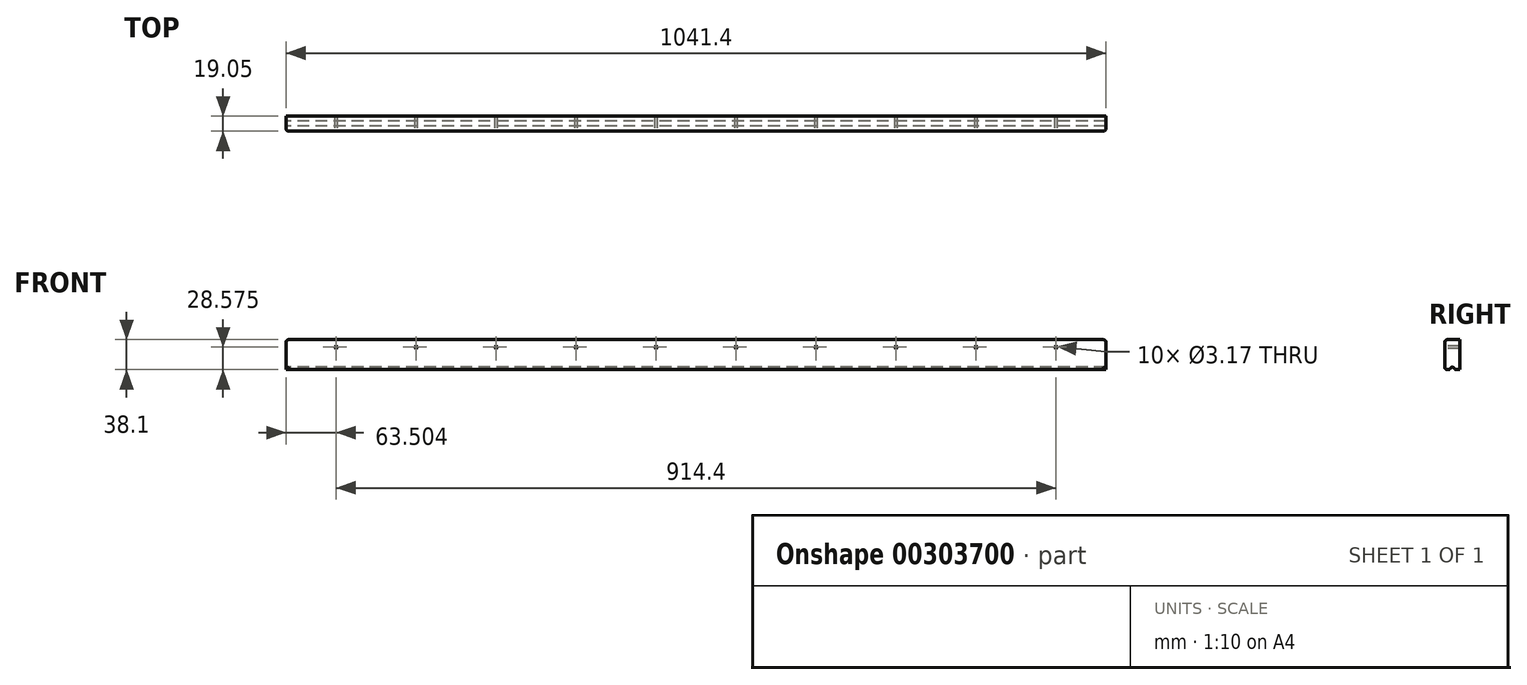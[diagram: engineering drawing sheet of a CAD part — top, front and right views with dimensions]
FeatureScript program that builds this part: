
annotation { "Feature Type Name" : "Feature", "Feature Type Description" : "" }
export const myFeature = defineFeature(function(context is Context, id is Id, definition is map)
    precondition{}
    {
        {
            var Q0;
            Q0=qCreatedBy(makeId("Front.planeOp"),FACE);
            var sketch = newSketch(context, id + "F0", { "sketchPlane" : qUnion([Q0])});
            skLineSegment(sketch, "E0.bottom", {"start": v(1.46, 0) * mm, "end": v(1042.86, 0) * mm});
            skLineSegment(sketch, "E0.top", {"start": v(1.46, -38.1) * mm, "end": v(1042.86, -38.1) * mm});
            skLineSegment(sketch, "E0.left", {"start": v(1.46, 0) * mm, "end": v(1.46, -38.1) * mm});
            skLineSegment(sketch, "E0.right", {"start": v(1042.86, 0) * mm, "end": v(1042.86, -38.1) * mm});
            skSolve(sketch);
        }
        {
            var Q0;
            Q0 = qSketchRegion(id + "F0", true);
            extrude(context, id + "F1", {"entities" : qUnion([Q0]), "oppositeDirection" : true, "depth" : 19.05 * mm});
        }
        {
            var Q0;
            Q0=qCreatedBy(makeId("Front.planeOp"),FACE);
            var sketch = newSketch(context, id + "F2", { "sketchPlane" : qUnion([Q0])});
            skCircle(sketch, "E1", {"center": v(64.96, -9.53) * mm, "radius": 1.59 * mm});
            skCircle(sketch, "E2.1.0.0", {"center": v(166.56, -9.53) * mm, "radius": 1.59 * mm});
            skCircle(sketch, "E2.2.0.0", {"center": v(268.16, -9.53) * mm, "radius": 1.59 * mm});
            skCircle(sketch, "E2.3.0.0", {"center": v(369.76, -9.53) * mm, "radius": 1.59 * mm});
            skCircle(sketch, "E2.4.0.0", {"center": v(471.36, -9.53) * mm, "radius": 1.59 * mm});
            skCircle(sketch, "E2.5.0.0", {"center": v(572.96, -9.53) * mm, "radius": 1.59 * mm});
            skCircle(sketch, "E2.6.0.0", {"center": v(674.56, -9.53) * mm, "radius": 1.59 * mm});
            skCircle(sketch, "E2.7.0.0", {"center": v(776.16, -9.53) * mm, "radius": 1.59 * mm});
            skCircle(sketch, "E2.8.0.0", {"center": v(877.76, -9.53) * mm, "radius": 1.59 * mm});
            skCircle(sketch, "E2.9.0.0", {"center": v(979.36, -9.53) * mm, "radius": 1.59 * mm});
            skLineSegment(sketch, "E2.direction1", {"start": v(64.96, -9.53) * mm, "end": v(166.56, -9.53) * mm, "construction": true});
            skSolve(sketch);
        }
        {
            var Q0;
            Q0 = qSketchRegion(id + "F2", true);
            extrude(context, id + "F3", {"entities" : qUnion([Q0]), "operationType" : NewBodyOperationType.REMOVE, "endBound" : BoundingType.THROUGH_ALL, "oppositeDirection" : true, "depth" : 25.4 * mm});
        }
        {
            var Q0;
            Q0=qCreatedBy(makeId("Right.planeOp"),FACE);
            var sketch = newSketch(context, id + "F4", { "sketchPlane" : qUnion([Q0])});
            skArc(sketch, "E3", {"start": v(12.7, -38.1) * mm, "mid": v(9.53, -34.93) * mm, "end": v(6.35, -38.1) * mm});
            skLineSegment(sketch, "E4", {"start": v(6.35, -38.1) * mm, "end": v(12.7, -38.1) * mm});
            skSolve(sketch);
        }
        {
            var Q0;
            Q0 = qSketchRegion(id + "F4", true);
            extrude(context, id + "F5", {"entities" : qUnion([Q0]), "operationType" : NewBodyOperationType.REMOVE, "endBound" : BoundingType.THROUGH_ALL, "depth" : 25.4 * mm});
        }
        {
            var Q0;
            {var subQ0=sQuery(id+"F4.wireOp",EDGE,"E4");var subQ1=sQuery(id+"F4.wireOp",EDGE,"E3");Q0=makeQuery(id+"F5.boolean.opBoolean","COPY",EDGE,{"derivedFrom":makeQuery(id+"F5.opExtrude","SWEPT_EDGE",EDGE,{"disambiguationData":[OSD([subQ1,subQ0]),TDD([makeQuery(id+"F4.imprint","INTERSECT",VERTEX,{"disambiguationData":[OD(1.0)],"derivedFrom":[subQ1,subQ0]})])]})});}
            var Q1;
            Q1=makeQuery(id+"F1.opExtrude","CAP_EDGE",EDGE,{"disambiguationData":[OSD([sQuery(id+"F0.wireOp",EDGE,"E0.top")])],"isStart":true});
            var Q2;
            Q2=makeQuery(id+"F1.opExtrude","CAP_EDGE",EDGE,{"disambiguationData":[OSD([sQuery(id+"F0.wireOp",EDGE,"E0.right")])],"isStart":true});
            var Q3;
            Q3=makeQuery(id+"F1.opExtrude","SWEPT_EDGE",EDGE,{"disambiguationData":[OSD([sQuery(id+"F0.wireOp",EDGE,"E0.bottom"),sQuery(id+"F0.wireOp",EDGE,"E0.right")])]});
            var Q4;
            Q4=makeQuery(id+"F1.opExtrude","CAP_EDGE",EDGE,{"disambiguationData":[OSD([sQuery(id+"F0.wireOp",EDGE,"E0.bottom")])],"isStart":true});
            var Q5;
            Q5=makeQuery(id+"F1.opExtrude","CAP_EDGE",EDGE,{"disambiguationData":[OSD([sQuery(id+"F0.wireOp",EDGE,"E0.left")])],"isStart":true});
            var Q6;
            Q6=makeQuery(id+"F1.opExtrude","SWEPT_EDGE",EDGE,{"disambiguationData":[OSD([sQuery(id+"F0.wireOp",EDGE,"E0.bottom"),sQuery(id+"F0.wireOp",EDGE,"E0.left")])]});
            fillet(context, id + "F6", {"entities" : qUnion([Q0, Q1, Q2, Q3, Q4, Q5, Q6]), "radius" : 3.17 * mm, "tangentPropagation" : true, "allowEdgeOverflow" : false});
        }
    });
